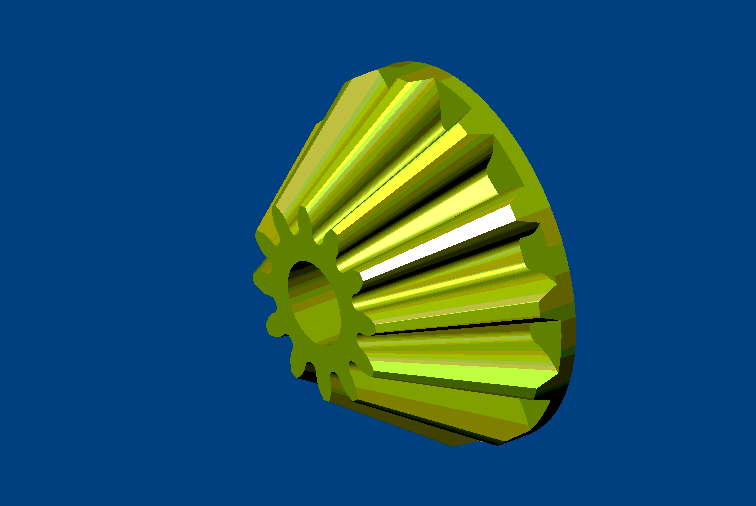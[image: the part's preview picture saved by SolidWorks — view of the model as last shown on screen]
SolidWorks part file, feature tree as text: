
SOLIDWORKS PART (.sldprt)
format: sldprt  version: not decoded by parser v0  size: 508,416 bytes
history: native  units: mm
features: sketch x22, plane x4, cut_extrude x2, extrude x2, material x1, fillet x1, pattern_circular x1 + 1 further entry (+9 scaffold rows collapsed)
feature tree (43):
  scaffold x9  (default folders/planes/origin — collapsed)
  material  "Matériau <non spécifié>"
  plane  "Plane1"
  plane  "Plane2"
  plane  "Plane3"
  "Famille de pièces"
  sketch  "Esquisse1"  dims[c1.D2=5.4mm c1.D1=42.0mm c2.D1=15.0deg]
  sketch  "Esquisse2"  dims[c1.D2=~5.291447mm c1.D1=37.0mm c2.D1=~15.769674deg]
  sketch  "Esquisse3"  dims[c1.D2=~5.182893mm c1.D1=33.0mm c2.D1=~16.373081deg]
  sketch  "Esquisse4"  dims[c1.D2=~5.07434mm c1.D1=30.0mm c2.D1=~16.707917deg]
  sketch  "Esquisse5"  dims[c1.D2=5.7mm c1.D1=46.0mm c2.D1=~12.269923deg]
  sketch  "Esquisse6"  dims[c1.D2=6.0mm c1.D1=50.0mm c2.D1=~8.905646deg]
  sketch  "Esquisse7"  dims[c1.D2=6.3mm c1.D1=54.0mm c2.D1=~5.082122deg]
  plane  "Plan1"  Offset=5mm
  sketch  "Esquisse8"  dims[c1.D2=~2.513249mm c1.D1=18.0mm c2.D1=15.0deg]
  sketch  "Esquisse9"  dims[c1.D2=~2.462726mm c1.D1=15.0mm c2.D1=~15.769674deg]
  sketch  "Esquisse10"  dims[c1.D2=~2.412204mm c1.D1=13.0mm c2.D1=~16.373081deg]
  sketch  "Esquisse11"  dims[c1.D2=~2.361681mm c1.D1=12.0mm c2.D1=~16.707917deg]
  sketch  "Esquisse12"  dims[c1.D2=~2.652874mm c1.D1=20.0mm c2.D1=~12.269923deg]
  sketch  "Esquisse13"  dims[c1.D2=~2.792499mm c1.D1=21.0mm c2.D1=~8.905646deg]
  sketch  "Esquisse14"  dims[c1.D2=~2.932123mm c1.D1=22.0mm c2.D1=~5.082122deg]
  sketch  "Esquisse15"  dims[c1.D2=4.275mm c1.D1=23.0mm c2.D1=~16.707917deg]
  sketch  "Esquisse16"  dims[c1.D2=~1.989655mm c1.D1=10.0mm c2.D1=~16.707917deg]
  sketch  "Esquisse17"  dims[D1=8.55mm]
  sketch  "Esquisse18"  dims[D1=~3.97931mm]
  fillet  "Congé1"  Radius=0.25mm
  pattern_circular  "Répétition circulaire1"  Count=12 Angle=360deg
  sketch  "Esquisse19"  dims[D1=2.5mm]
  sketch  "Esquisse20"  dims[D1=11.0mm]
  cut_extrude  "Enlèv. mat.-Extru.2"  [1 undecoded]
  sketch  "Esquisse21"
  extrude  "Boss.-Extru.1"  Depth=0.5mm
  sketch  "Esquisse22"  dims[D1=5.0mm]
  extrude  "Boss.-Extru.2"  Depth=0.25mm
  cut_extrude  "Enlèv. mat.-Extru.3"  [1 undecoded]
decode coverage: 25 of 28 modeling features carry decoded parameters; 1 rows unclassified (native names shown)
note: ~ marks probable driven/reference dimensions
note: 2 parameter values undecoded
note: suppression state not decoded; provenance and decode notes live in map.json
